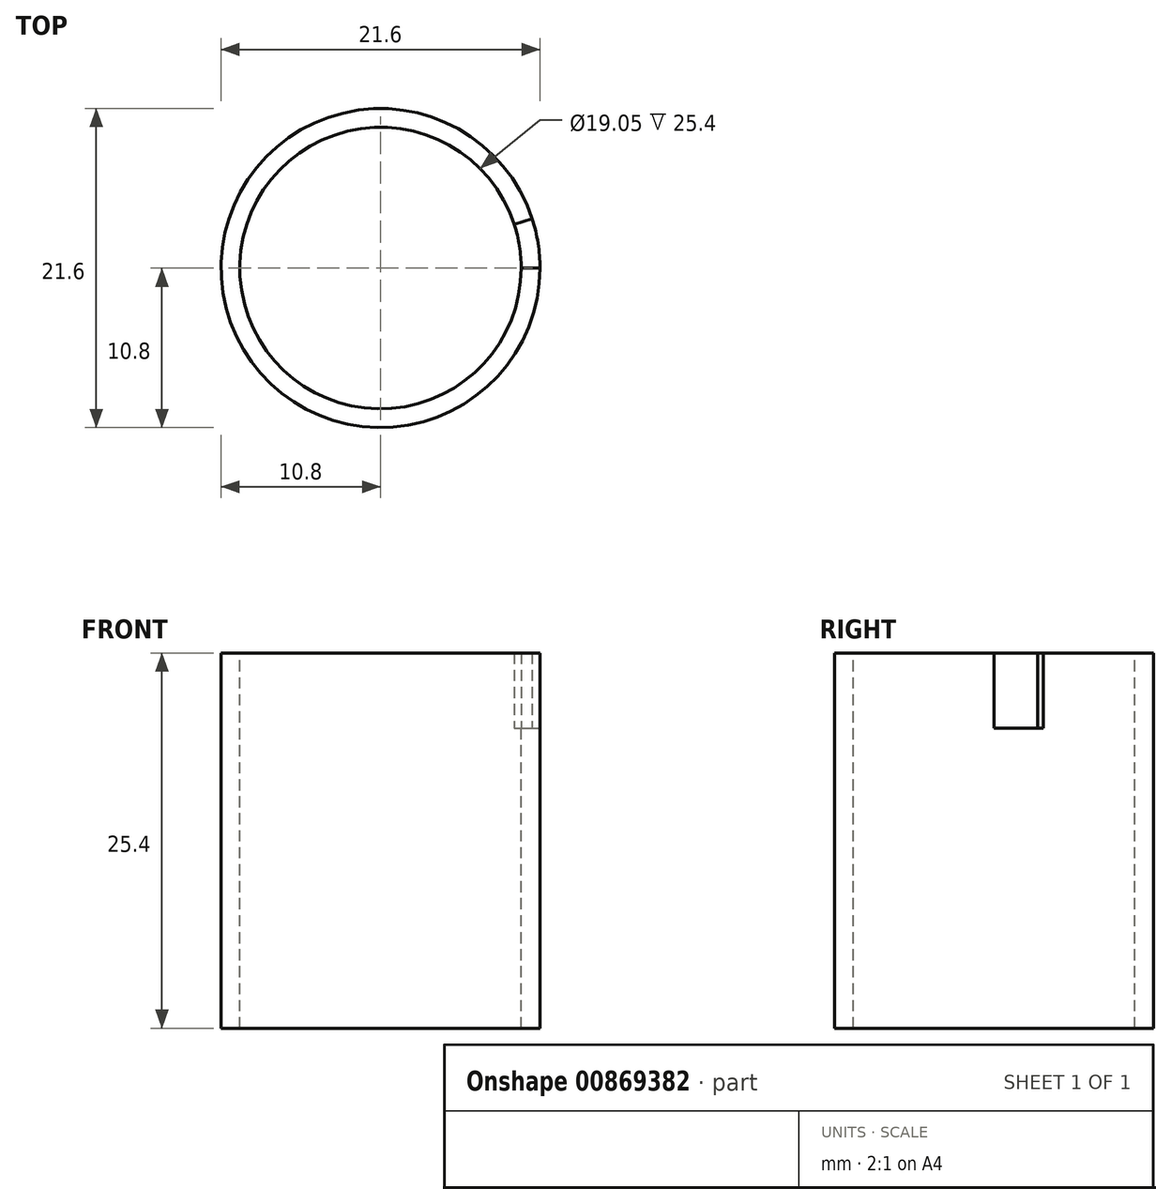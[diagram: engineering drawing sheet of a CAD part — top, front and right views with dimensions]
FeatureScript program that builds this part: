
annotation { "Feature Type Name" : "Feature", "Feature Type Description" : "" }
export const myFeature = defineFeature(function(context is Context, id is Id, definition is map)
    precondition{}
    {
        {
            var Q0;
            Q0=qCreatedBy(makeId("Front.planeOp"),FACE);
            var sketch = newSketch(context, id + "F0", { "sketchPlane" : qUnion([Q0])});
            skLineSegment(sketch, "E0", {"start": v(0, 13.2) * mm, "end": v(0, -11.6) * mm, "construction": true});
            skLineSegment(sketch, "E1.bottom", {"start": v(9.53, 12.7) * mm, "end": v(10.8, 12.7) * mm});
            skLineSegment(sketch, "E1.top", {"start": v(9.53, -12.7) * mm, "end": v(10.8, -12.7) * mm});
            skLineSegment(sketch, "E1.left", {"start": v(9.53, 12.7) * mm, "end": v(9.53, -12.7) * mm});
            skLineSegment(sketch, "E1.right", {"start": v(10.8, 12.7) * mm, "end": v(10.8, -12.7) * mm});
            skSolve(sketch);
        }
        {
            var Q0;
            Q0 = qSketchRegion(id + "F0", true);
            var Q1;
            Q1=sQuery(id+"F0.wireOp",EDGE,"E0");
            revolve(context, id + "F1", {"surfaceOperationType" : NewSurfaceOperationType.NEW, "entities" : qUnion([Q0]), "axis" : qUnion([Q1]), "revolveType" : RevolveType.SYMMETRIC, "angle" : 360 * degree});
        }
        {
            var Q0;
            Q0=qCreatedBy(makeId("Front.planeOp"),FACE);
            var sketch = newSketch(context, id + "F2", { "sketchPlane" : qUnion([Q0])});
            skLineSegment(sketch, "E2.bottom", {"start": v(9.53, 12.7) * mm, "end": v(10.8, 12.7) * mm});
            skLineSegment(sketch, "E2.top", {"start": v(9.53, 7.62) * mm, "end": v(10.8, 7.62) * mm});
            skLineSegment(sketch, "E2.left", {"start": v(9.53, 12.7) * mm, "end": v(9.53, 7.62) * mm});
            skLineSegment(sketch, "E2.right", {"start": v(10.8, 12.7) * mm, "end": v(10.8, 7.62) * mm});
            skSolve(sketch);
        }
        {
            var Q0;
            Q0 = qSketchRegion(id + "F2", true);
            var Q1;
            Q1=makeQuery(id+"F1.opRevolve","SWEPT_EDGE",EDGE,{"disambiguationData":[OSD([sQuery(id+"F0.wireOp",EDGE,"E1.bottom"),sQuery(id+"F0.wireOp",EDGE,"E1.right")])]});
            revolve(context, id + "F3", {"operationType" : NewBodyOperationType.REMOVE, "surfaceOperationType" : NewSurfaceOperationType.NEW, "entities" : qUnion([Q0]), "axis" : qUnion([Q1]), "revolveType" : RevolveType.ONE_DIRECTION, "angle" : 18 * degree});
        }
        {
            var Q0;
            Q0=makeQuery(id+"F1.opRevolve","SWEPT_FACE",FACE,{"disambiguationData":[OSD([sQuery(id+"F0.wireOp",EDGE,"E1.bottom")])]});
            var sketch = newSketch(context, id + "F4", { "sketchPlane" : qUnion([Q0])});
            skCircle(sketch, "E3", {"center": v(0, 0) * mm, "radius": 10.16 * mm, "construction": true});
            skSolve(sketch);
        }
    });
